# Revit family: Дио_мини
name_source: partatom
category: Осветительные приборы
units: mm (PartAtom-declared; Revit-internal decimal feet)

## family parameters
Всегда вертикально = Да
Источник света = Да
На основе рабочей плоскости = Нет
Общий = Нет
При загрузке вырезать с полостями = Нет
Размер круглого соединителя = Использовать диаметр
Тип детали = Нормальный
Точка расчета площади = Нет

## types (1)
- ДТУ932 Светодиодный светильник Дио мини ДТУ-93-AF-12Вт-0,9
    ADSK_URL страницы изделия = https://www.allfresco.ru
    ADSK_Артикул = ДТУ932
    ADSK_Единица измерения = шт.
    ADSK_Завод-изготовитель = ALFRESCO
    ADSK_Количество фаз = 2
    ADSK_Количество фаз числовое = 0
    ADSK_Коэффициент мощности = 0
    ADSK_Масса = 8
    ADSK_Масса_Текст = 8
    ADSK_Модель = Дио мини ДТУ-93-AF
    ADSK_Наименование = ДТУ932 Светодиодный светильник Дио мини ДТУ-93-AF-12Вт-0.9
    ADSK_Напряжение = 220 В
    ADSK_Номинальная мощность = 12 Вт
    ADSK_Полная мощность = 0 В·А
    ADSK_Размер_Высота = 900 мм
    ADSK_Ток = 0 А
    ADSK_Фактическая мощность = 10 Вт
    ADSK_Энергоэффективность = 110 лм/Вт
    Angle = 45.00°
    D_столб = 89 мм
    D_фланец = 150 мм
    H_дверка = 860 мм
    H_конечной точки = 1500 мм
    H_столб = 570 мм
    H_точки освещения = 170 мм
    H_фланец = 6 мм
    IP Class = IP 67
    L_отступ до конечной точки = 1500 мм
    L_отступ до центра = 1000 мм
    L_поворот = 164 мм
    R_поворот = 120 мм
    R_поворот столба = 95 мм
    R_столб = 45 мм
    a_отступ точки освещения = 170 мм
    Блок аварийного питания = Нет
    Класс защиты = 1
    Класс пожароопасности = F (светильники предназначены для установки непосредственно на поверхность из нормально воспламеняемых материалов)
    Климатическая зона = УХЛ1
    Короб_Диаметр = 20 мм
    Корпус светильника = Антрацит
    Материал рассеивателя = Светотехнический ПК
    Область использования = Парки, скверы, общественные пространства, городская инфраструктура
    Полная установленная мощность = 0 В·А
    Понижение = 330 мм
    Рассеиватель = Белый_светодиод
    Светофильтр = 16777215
    Смещение цветовой температуры при затухании лампы = <Нет>
    Таблица выбора = Таблица параметров светильников_par2
    Температура эксплуатации = -40 +50
    Тип ИС = LED-модуль
    Тип КСС = тип ШБ (широкая боковая)
    Тип ПРА = -
    Тип продукции = LED-светильник
    Угол наклона = 90.00°
    Файл фотометрической сетки = DTU-93-AF Dio mini 12W.ies
    Цветоывая температура = 2700-5500

## geometry (parser evidence)
native form markers: Blend x2
no freeform markers — native parametric forms only
